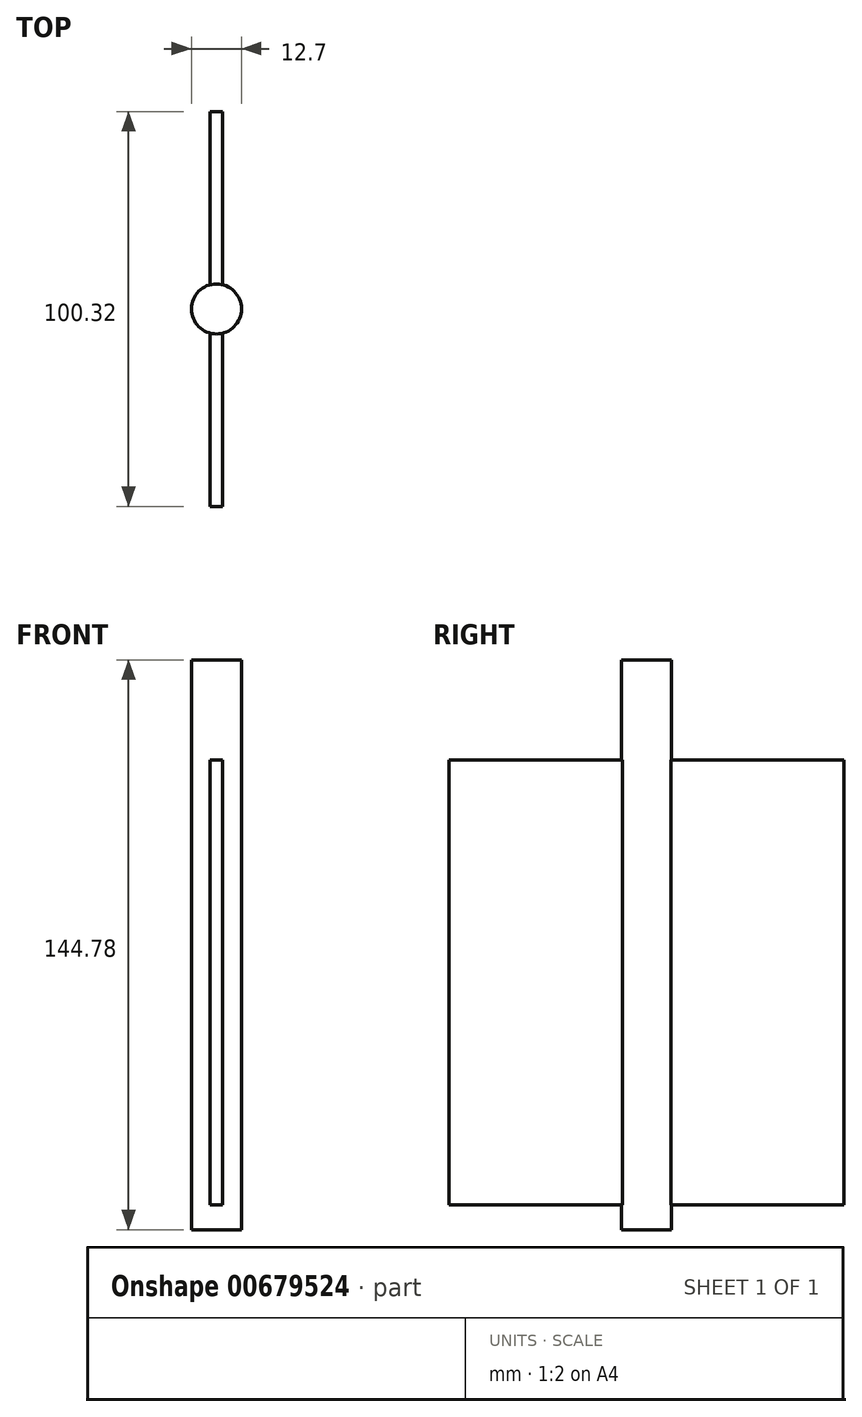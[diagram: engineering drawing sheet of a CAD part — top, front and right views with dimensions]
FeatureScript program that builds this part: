
annotation { "Feature Type Name" : "Feature", "Feature Type Description" : "" }
export const myFeature = defineFeature(function(context is Context, id is Id, definition is map)
    precondition{}
    {
        {
            var Q0;
            Q0=qCreatedBy(makeId("Top.planeOp"),FACE);
            var sketch = newSketch(context, id + "F0", { "sketchPlane" : qUnion([Q0])});
            skArc(sketch, "E0", {"start": v(-1.59, 6.15) * mm, "mid": v(-6.35, 0) * mm, "end": v(-1.59, -6.15) * mm});
            skLineSegment(sketch, "E1.bottom", {"start": v(-1.59, -50.17) * mm, "end": v(1.59, -50.17) * mm});
            skLineSegment(sketch, "E1.top", {"start": v(-1.59, 50.17) * mm, "end": v(1.59, 50.17) * mm});
            skLineSegment(sketch, "E1.left", {"start": v(-1.59, -50.17) * mm, "end": v(-1.59, -6.15) * mm});
            skLineSegment(sketch, "E1.right", {"start": v(1.59, -50.17) * mm, "end": v(1.59, -6.15) * mm});
            skArc(sketch, "E2.trimOffspring", {"start": v(1.59, -6.15) * mm, "mid": v(6.35, 0) * mm, "end": v(1.59, 6.15) * mm});
            skLineSegment(sketch, "E3.trimOffspring", {"start": v(-1.59, 6.15) * mm, "end": v(-1.59, 50.17) * mm});
            skLineSegment(sketch, "E4.trimOffspring", {"start": v(1.59, 6.15) * mm, "end": v(1.59, 50.17) * mm});
            skSolve(sketch);
        }
        {
            var Q0;
            Q0 = qSketchRegion(id + "F0", true);
            extrude(context, id + "F1", {"entities" : qUnion([Q0]), "depth" : 113.03 * mm, "offsetDistance" : 25.4 * mm});
        }
        {
            var Q0;
            Q0=makeQuery(id+"F1.opExtrude","CAP_FACE",FACE,{"disambiguationData":[OSD([sQuery(id+"F0.wireOp",EDGE,"E0"),sQuery(id+"F0.wireOp",EDGE,"E1.bottom"),sQuery(id+"F0.wireOp",EDGE,"E1.top"),sQuery(id+"F0.wireOp",EDGE,"E1.left"),sQuery(id+"F0.wireOp",EDGE,"E1.right"),sQuery(id+"F0.wireOp",EDGE,"E2.trimOffspring"),sQuery(id+"F0.wireOp",EDGE,"E3.trimOffspring"),sQuery(id+"F0.wireOp",EDGE,"E4.trimOffspring")])],"isStart":true});
            var sketch = newSketch(context, id + "F2", { "sketchPlane" : qUnion([Q0])});
            skCircle(sketch, "E5", {"center": v(0, 0) * mm, "radius": 6.35 * mm});
            skSolve(sketch);
        }
        {
            var Q0;
            Q0 = qSketchRegion(id + "F2", true);
            extrude(context, id + "F3", {"entities" : qUnion([Q0]), "operationType" : NewBodyOperationType.ADD, "depth" : 6.35 * mm, "offsetDistance" : 25.4 * mm});
        }
        {
            var Q0;
            Q0=makeQuery(id+"F1.opExtrude","CAP_FACE",FACE,{"disambiguationData":[OSD([sQuery(id+"F0.wireOp",EDGE,"E0"),sQuery(id+"F0.wireOp",EDGE,"E1.bottom"),sQuery(id+"F0.wireOp",EDGE,"E1.top"),sQuery(id+"F0.wireOp",EDGE,"E1.left"),sQuery(id+"F0.wireOp",EDGE,"E1.right"),sQuery(id+"F0.wireOp",EDGE,"E2.trimOffspring"),sQuery(id+"F0.wireOp",EDGE,"E3.trimOffspring"),sQuery(id+"F0.wireOp",EDGE,"E4.trimOffspring")])],"isStart":false});
            var sketch = newSketch(context, id + "F4", { "sketchPlane" : qUnion([Q0])});
            skCircle(sketch, "E6", {"center": v(0, 0) * mm, "radius": 6.35 * mm});
            skSolve(sketch);
        }
        {
            var Q0;
            Q0 = qSketchRegion(id + "F4", true);
            extrude(context, id + "F5", {"entities" : qUnion([Q0]), "operationType" : NewBodyOperationType.ADD, "depth" : 25.4 * mm, "offsetDistance" : 25.4 * mm});
        }
    });
